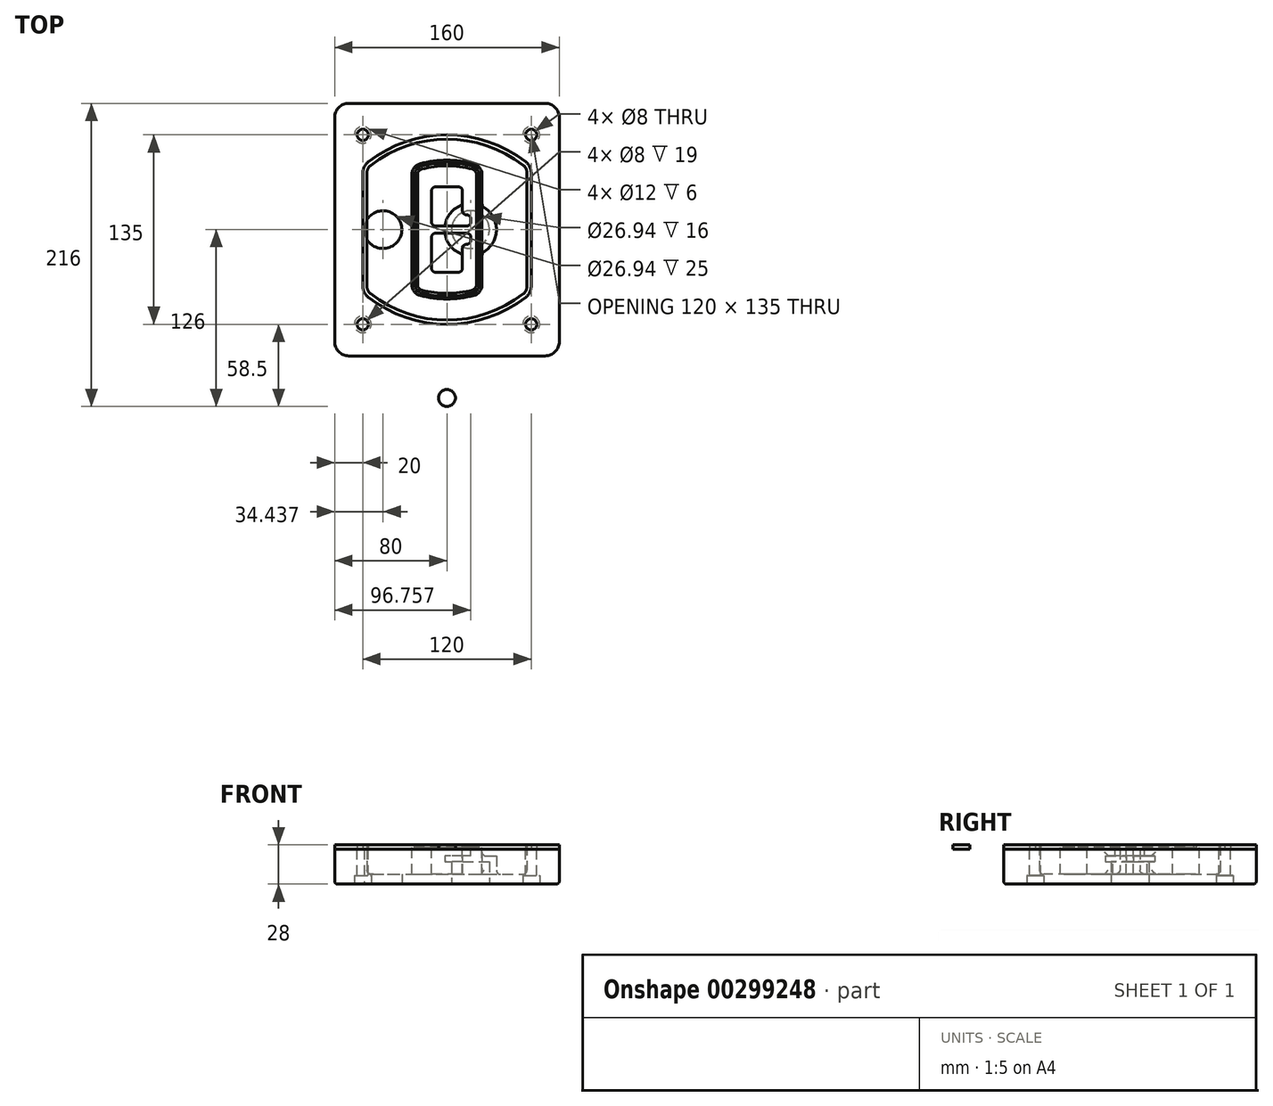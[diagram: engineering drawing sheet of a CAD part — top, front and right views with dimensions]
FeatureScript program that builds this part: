
annotation { "Feature Type Name" : "Feature", "Feature Type Description" : "" }
export const myFeature = defineFeature(function(context is Context, id is Id, definition is map)
    precondition{}
    {
        {
            var Q0;
            Q0=qCreatedBy(makeId("Top.planeOp"),FACE);
            var sketch = newSketch(context, id + "F0", { "sketchPlane" : qUnion([Q0])});
            skPoint(sketch, "E0.rect.middle", {"position": v(0, 0) * mm});
            skLineSegment(sketch, "E1.bottom", {"start": v(-70, -90) * mm, "end": v(70, -90) * mm});
            skLineSegment(sketch, "E1.top", {"start": v(-70, 90) * mm, "end": v(70, 90) * mm});
            skLineSegment(sketch, "E1.left", {"start": v(-80, -80) * mm, "end": v(-80, 80) * mm});
            skLineSegment(sketch, "E1.right", {"start": v(80, -80) * mm, "end": v(80, 80) * mm});
            skLineSegment(sketch, "E2", {"start": v(-80, 90) * mm, "end": v(80, -90) * mm, "construction": true});
            skLineSegment(sketch, "E3", {"start": v(80, 90) * mm, "end": v(-80, -90) * mm, "construction": true});
            skCircle(sketch, "E4", {"center": v(-60, 67.5) * mm, "radius": 4 * mm});
            skCircle(sketch, "E5", {"center": v(60, 67.5) * mm, "radius": 4 * mm});
            skCircle(sketch, "E6", {"center": v(60, -67.5) * mm, "radius": 4 * mm});
            skCircle(sketch, "E7", {"center": v(-60, -67.5) * mm, "radius": 4 * mm});
            skLineSegment(sketch, "E8", {"start": v(-60, 67.5) * mm, "end": v(60, 67.5) * mm, "construction": true});
            skLineSegment(sketch, "E9", {"start": v(60, 67.5) * mm, "end": v(60, -67.5) * mm, "construction": true});
            skLineSegment(sketch, "E10", {"start": v(60, -67.5) * mm, "end": v(-60, -67.5) * mm, "construction": true});
            skLineSegment(sketch, "E11", {"start": v(-60, -67.5) * mm, "end": v(-60, 67.5) * mm, "construction": true});
            skLineSegment(sketch, "E12", {"start": v(-60, 40.3) * mm, "end": v(-60, -40.3) * mm});
            skLineSegment(sketch, "E13", {"start": v(60, 40.3) * mm, "end": v(60, -40.3) * mm});
            skArc(sketch, "E14", {"start": v(56.15, 48.18) * mm, "mid": v(0, 67.5) * mm, "end": v(-56.15, 48.18) * mm});
            skArc(sketch, "E15", {"start": v(-56.15, -48.18) * mm, "mid": v(0, -67.5) * mm, "end": v(56.15, -48.18) * mm});
            skLineSegment(sketch, "E16", {"start": v(-60, 0) * mm, "end": v(60, 0) * mm, "construction": true});
            skPoint(sketch, "E17.visualSharp", {"position": v(-60, -45) * mm});
            skArc(sketch, "E17.filletArc", {"start": v(-60, -40.3) * mm, "mid": v(-58.99, -44.68) * mm, "end": v(-56.15, -48.18) * mm});
            skPoint(sketch, "E18.visualSharp", {"position": v(-60, 45) * mm});
            skArc(sketch, "E18.filletArc", {"start": v(-56.15, 48.18) * mm, "mid": v(-58.99, 44.68) * mm, "end": v(-60, 40.3) * mm});
            skPoint(sketch, "E19.visualSharp", {"position": v(60, 45) * mm});
            skArc(sketch, "E19.filletArc", {"start": v(60, 40.3) * mm, "mid": v(58.99, 44.68) * mm, "end": v(56.15, 48.18) * mm});
            skPoint(sketch, "E20.visualSharp", {"position": v(60, -45) * mm});
            skArc(sketch, "E20.filletArc", {"start": v(56.15, -48.18) * mm, "mid": v(58.99, -44.68) * mm, "end": v(60, -40.3) * mm});
            skPoint(sketch, "E21.visualSharp", {"position": v(-80, 90) * mm});
            skArc(sketch, "E21.filletArc", {"start": v(-70, 90) * mm, "mid": v(-77.07, 87.07) * mm, "end": v(-80, 80) * mm});
            skPoint(sketch, "E22.visualSharp", {"position": v(80, 90) * mm});
            skArc(sketch, "E22.filletArc", {"start": v(80, 80) * mm, "mid": v(77.07, 87.07) * mm, "end": v(70, 90) * mm});
            skPoint(sketch, "E23.visualSharp", {"position": v(80, -90) * mm});
            skArc(sketch, "E23.filletArc", {"start": v(70, -90) * mm, "mid": v(77.07, -87.07) * mm, "end": v(80, -80) * mm});
            skPoint(sketch, "E24.visualSharp", {"position": v(-80, -90) * mm});
            skArc(sketch, "E24.filletArc", {"start": v(-80, -80) * mm, "mid": v(-77.07, -87.07) * mm, "end": v(-70, -90) * mm});
            skArc(sketch, "E25.0", {"start": v(57, 40.3) * mm, "mid": v(56.3, 43.36) * mm, "end": v(54.3, 45.81) * mm});
            skLineSegment(sketch, "E25.1", {"start": v(57, 40.3) * mm, "end": v(57, -40.3) * mm});
            skArc(sketch, "E25.2", {"start": v(54.3, -45.81) * mm, "mid": v(56.3, -43.36) * mm, "end": v(57, -40.3) * mm});
            skArc(sketch, "E25.3", {"start": v(-54.3, -45.81) * mm, "mid": v(0, -64.5) * mm, "end": v(54.3, -45.81) * mm});
            skArc(sketch, "E25.4", {"start": v(-57, -40.3) * mm, "mid": v(-56.3, -43.36) * mm, "end": v(-54.3, -45.81) * mm});
            skArc(sketch, "E25.5", {"start": v(54.3, 45.81) * mm, "mid": v(0, 64.5) * mm, "end": v(-54.3, 45.81) * mm});
            skLineSegment(sketch, "E25.6", {"start": v(-57, 40.3) * mm, "end": v(-57, -40.3) * mm});
            skArc(sketch, "E25.7", {"start": v(-54.3, 45.81) * mm, "mid": v(-56.3, 43.36) * mm, "end": v(-57, 40.3) * mm});
            skArc(sketch, "E26.0", {"start": v(-58.62, 51.33) * mm, "mid": v(-62.58, 46.43) * mm, "end": v(-64, 40.3) * mm});
            skArc(sketch, "E26.1", {"start": v(58.62, 51.33) * mm, "mid": v(0, 71.5) * mm, "end": v(-58.62, 51.33) * mm});
            skArc(sketch, "E26.2", {"start": v(64, 40.3) * mm, "mid": v(62.58, 46.43) * mm, "end": v(58.62, 51.33) * mm});
            skLineSegment(sketch, "E26.3", {"start": v(64, 40.3) * mm, "end": v(64, -40.3) * mm});
            skArc(sketch, "E26.4", {"start": v(58.62, -51.33) * mm, "mid": v(62.58, -46.43) * mm, "end": v(64, -40.3) * mm});
            skLineSegment(sketch, "E26.5", {"start": v(-64, 40.3) * mm, "end": v(-64, -40.3) * mm});
            skArc(sketch, "E26.6", {"start": v(-58.62, -51.33) * mm, "mid": v(0, -71.5) * mm, "end": v(58.62, -51.33) * mm});
            skArc(sketch, "E26.7", {"start": v(-64, -40.3) * mm, "mid": v(-62.58, -46.43) * mm, "end": v(-58.62, -51.33) * mm});
            skSolve(sketch);
        }
        {
            var Q0;
            Q0=makeQuery(id+"F0.imprint","IMPRINT",FACE,{"disambiguationData":[TD([[makeQuery(id+"F0.imprint","IMPRINT",EDGE,{"derivedFrom":sQuery(id+"F0.wireOp",EDGE,"E1.bottom")}),1.0]])]});
            var Q1;
            Q1=makeQuery(id+"F0.imprint","IMPRINT",FACE,{"disambiguationData":[TD([[makeQuery(id+"F0.imprint","IMPRINT",EDGE,{"derivedFrom":sQuery(id+"F0.wireOp",EDGE,"E12")}),1.0]])]});
            var Q2;
            Q2=makeQuery(id+"F0.imprint","IMPRINT",FACE,{"disambiguationData":[TD([[makeQuery(id+"F0.imprint","IMPRINT",EDGE,{"derivedFrom":sQuery(id+"F0.wireOp",EDGE,"E25.0")}),1.0]])]});
            var Q3;
            Q3=makeQuery(id+"F0.imprint","IMPRINT",FACE,{"disambiguationData":[TD([[makeQuery(id+"F0.imprint","IMPRINT",EDGE,{"derivedFrom":sQuery(id+"F0.wireOp",EDGE,"E12")}),-1.0]])]});
            extrude(context, id + "F1", {"entities" : qUnion([Q0, Q1, Q2, Q3]), "oppositeDirection" : true, "depth" : 25 * mm});
        }
        {
            var Q0;
            Q0=makeQuery(id+"F0.imprint","IMPRINT",FACE,{"disambiguationData":[TD([[makeQuery(id+"F0.imprint","IMPRINT",EDGE,{"derivedFrom":sQuery(id+"F0.wireOp",EDGE,"E12")}),1.0]])]});
            extrude(context, id + "F2", {"entities" : qUnion([Q0]), "operationType" : NewBodyOperationType.ADD, "depth" : 3 * mm});
        }
        {
            var Q0;
            Q0=makeQuery(id+"F0.imprint","IMPRINT",FACE,{"disambiguationData":[TD([[makeQuery(id+"F0.imprint","IMPRINT",EDGE,{"derivedFrom":sQuery(id+"F0.wireOp",EDGE,"E25.0")}),1.0]])]});
            extrude(context, id + "F3", {"entities" : qUnion([Q0]), "operationType" : NewBodyOperationType.REMOVE, "oppositeDirection" : true, "depth" : 18 * mm});
        }
        {
            var Q0;
            Q0=makeQuery(id+"F2.opExtrude","CAP_FACE",FACE,{"disambiguationData":[OSD([sQuery(id+"F0.wireOp",EDGE,"E12"),sQuery(id+"F0.wireOp",EDGE,"E13"),sQuery(id+"F0.wireOp",EDGE,"E14"),sQuery(id+"F0.wireOp",EDGE,"E15"),sQuery(id+"F0.wireOp",EDGE,"E17.filletArc"),sQuery(id+"F0.wireOp",EDGE,"E18.filletArc"),sQuery(id+"F0.wireOp",EDGE,"E19.filletArc"),sQuery(id+"F0.wireOp",EDGE,"E20.filletArc"),sQuery(id+"F0.wireOp",EDGE,"E25.0"),sQuery(id+"F0.wireOp",EDGE,"E25.1"),sQuery(id+"F0.wireOp",EDGE,"E25.2"),sQuery(id+"F0.wireOp",EDGE,"E25.3"),sQuery(id+"F0.wireOp",EDGE,"E25.4"),sQuery(id+"F0.wireOp",EDGE,"E25.5"),sQuery(id+"F0.wireOp",EDGE,"E25.6"),sQuery(id+"F0.wireOp",EDGE,"E25.7")])],"isStart":false});
            var sketch = newSketch(context, id + "F4", { "sketchPlane" : qUnion([Q0])});
            skArc(sketch, "E27.0", {"start": v(-19.08, -46.97) * mm, "mid": v(0, -49.5) * mm, "end": v(19.08, -46.97) * mm});
            skArc(sketch, "E28.0", {"start": v(19.08, 46.97) * mm, "mid": v(0, 49.5) * mm, "end": v(-19.08, 46.97) * mm});
            skLineSegment(sketch, "E29", {"start": v(-25, 39.25) * mm, "end": v(-25, -39.25) * mm});
            skLineSegment(sketch, "E30", {"start": v(25, 39.25) * mm, "end": v(25, -39.25) * mm});
            skLineSegment(sketch, "E31", {"start": v(-25, 45.1) * mm, "end": v(25, 45.1) * mm, "construction": true});
            skLineSegment(sketch, "E32", {"start": v(-25, -45.1) * mm, "end": v(25, -45.1) * mm, "construction": true});
            skPoint(sketch, "E33.visualSharp", {"position": v(-25, 45.1) * mm});
            skArc(sketch, "E33.filletArc", {"start": v(-19.08, 46.97) * mm, "mid": v(-23.35, 44.11) * mm, "end": v(-25, 39.25) * mm});
            skPoint(sketch, "E34.visualSharp", {"position": v(25, 45.1) * mm});
            skArc(sketch, "E34.filletArc", {"start": v(25, 39.25) * mm, "mid": v(23.35, 44.11) * mm, "end": v(19.08, 46.97) * mm});
            skPoint(sketch, "E35.visualSharp", {"position": v(25, -45.1) * mm});
            skArc(sketch, "E35.filletArc", {"start": v(19.08, -46.97) * mm, "mid": v(23.35, -44.11) * mm, "end": v(25, -39.25) * mm});
            skPoint(sketch, "E36.visualSharp", {"position": v(-25, -45.1) * mm});
            skArc(sketch, "E36.filletArc", {"start": v(-25, -39.25) * mm, "mid": v(-23.35, -44.11) * mm, "end": v(-19.08, -46.97) * mm});
            skArc(sketch, "E37.0", {"start": v(54.3, 45.81) * mm, "mid": v(0, 64.5) * mm, "end": v(-54.3, 45.81) * mm});
            skArc(sketch, "E37.1", {"start": v(-54.3, 45.81) * mm, "mid": v(-56.3, 43.36) * mm, "end": v(-57, 40.3) * mm});
            skLineSegment(sketch, "E37.2", {"start": v(-57, 40.3) * mm, "end": v(-57, -40.3) * mm});
            skArc(sketch, "E37.3", {"start": v(-57, -40.3) * mm, "mid": v(-56.3, -43.36) * mm, "end": v(-54.3, -45.81) * mm});
            skArc(sketch, "E37.4", {"start": v(-54.3, -45.81) * mm, "mid": v(0, -64.5) * mm, "end": v(54.3, -45.81) * mm});
            skArc(sketch, "E37.5", {"start": v(54.3, -45.81) * mm, "mid": v(56.3, -43.36) * mm, "end": v(57, -40.3) * mm});
            skLineSegment(sketch, "E37.6", {"start": v(57, 40.3) * mm, "end": v(57, -40.3) * mm});
            skArc(sketch, "E37.7", {"start": v(57, 40.3) * mm, "mid": v(56.3, 43.36) * mm, "end": v(54.3, 45.81) * mm});
            skLineSegment(sketch, "E38.0", {"start": v(23, 39.25) * mm, "end": v(23, -39.25) * mm});
            skArc(sketch, "E38.1", {"start": v(18.56, -45.04) * mm, "mid": v(21.76, -42.9) * mm, "end": v(23, -39.25) * mm});
            skArc(sketch, "E38.2", {"start": v(-18.56, -45.04) * mm, "mid": v(0, -47.5) * mm, "end": v(18.56, -45.04) * mm});
            skArc(sketch, "E38.3", {"start": v(-23, -39.25) * mm, "mid": v(-21.76, -42.9) * mm, "end": v(-18.56, -45.04) * mm});
            skLineSegment(sketch, "E38.4", {"start": v(-23, 39.25) * mm, "end": v(-23, -39.25) * mm});
            skArc(sketch, "E38.5", {"start": v(23, 39.25) * mm, "mid": v(21.76, 42.9) * mm, "end": v(18.56, 45.04) * mm});
            skArc(sketch, "E38.6", {"start": v(-18.56, 45.04) * mm, "mid": v(-21.76, 42.9) * mm, "end": v(-23, 39.25) * mm});
            skArc(sketch, "E38.7", {"start": v(18.56, 45.04) * mm, "mid": v(0, 47.5) * mm, "end": v(-18.56, 45.04) * mm});
            skArc(sketch, "E39.0", {"start": v(21, 39.25) * mm, "mid": v(20.18, 41.68) * mm, "end": v(18.04, 43.1) * mm});
            skLineSegment(sketch, "E39.1", {"start": v(21, 39.25) * mm, "end": v(21, -39.25) * mm});
            skArc(sketch, "E39.2", {"start": v(18.04, -43.1) * mm, "mid": v(20.18, -41.68) * mm, "end": v(21, -39.25) * mm});
            skArc(sketch, "E39.3", {"start": v(-18.04, -43.1) * mm, "mid": v(0, -45.5) * mm, "end": v(18.04, -43.1) * mm});
            skArc(sketch, "E39.4", {"start": v(-21, -39.25) * mm, "mid": v(-20.18, -41.68) * mm, "end": v(-18.04, -43.1) * mm});
            skArc(sketch, "E39.5", {"start": v(18.04, 43.1) * mm, "mid": v(0, 45.5) * mm, "end": v(-18.04, 43.1) * mm});
            skLineSegment(sketch, "E39.6", {"start": v(-21, 39.25) * mm, "end": v(-21, -39.25) * mm});
            skArc(sketch, "E39.7", {"start": v(-18.04, 43.1) * mm, "mid": v(-20.18, 41.68) * mm, "end": v(-21, 39.25) * mm});
            skLineSegment(sketch, "E40", {"start": v(-25, 0) * mm, "end": v(25, 0) * mm, "construction": true});
            skLineSegment(sketch, "E41", {"start": v(-11, 5.5) * mm, "end": v(-11, 27.5) * mm});
            skLineSegment(sketch, "E42", {"start": v(-8, 30.5) * mm, "end": v(8, 30.5) * mm});
            skLineSegment(sketch, "E43", {"start": v(11, 27.5) * mm, "end": v(11, 13.5) * mm});
            skLineSegment(sketch, "E44", {"start": v(14, 10.5) * mm, "end": v(14, 10.5) * mm});
            skLineSegment(sketch, "E45", {"start": v(17, 7.5) * mm, "end": v(17, 5.5) * mm});
            skLineSegment(sketch, "E46", {"start": v(14, 2.5) * mm, "end": v(-8, 2.5) * mm});
            skPoint(sketch, "E47.visualSharp", {"position": v(-11, 30.5) * mm});
            skArc(sketch, "E47.filletArc", {"start": v(-8, 30.5) * mm, "mid": v(-10.12, 29.62) * mm, "end": v(-11, 27.5) * mm});
            skPoint(sketch, "E48.visualSharp", {"position": v(11, 30.5) * mm});
            skArc(sketch, "E48.filletArc", {"start": v(11, 27.5) * mm, "mid": v(10.12, 29.62) * mm, "end": v(8, 30.5) * mm});
            skPoint(sketch, "E49.visualSharp", {"position": v(11, 10.5) * mm});
            skArc(sketch, "E49.filletArc", {"start": v(11, 13.5) * mm, "mid": v(11.88, 11.38) * mm, "end": v(14, 10.5) * mm});
            skPoint(sketch, "E50.visualSharp", {"position": v(17, 10.5) * mm});
            skArc(sketch, "E50.filletArc", {"start": v(17, 7.5) * mm, "mid": v(16.12, 9.62) * mm, "end": v(14, 10.5) * mm});
            skPoint(sketch, "E51.visualSharp", {"position": v(17, 2.5) * mm});
            skArc(sketch, "E51.filletArc", {"start": v(14, 2.5) * mm, "mid": v(16.12, 3.38) * mm, "end": v(17, 5.5) * mm});
            skPoint(sketch, "E52.visualSharp", {"position": v(-11, 2.5) * mm});
            skArc(sketch, "E52.filletArc", {"start": v(-11, 5.5) * mm, "mid": v(-10.12, 3.38) * mm, "end": v(-8, 2.5) * mm});
            skLineSegment(sketch, "E53.0.MirrorCS", {"start": v(14, -2.5) * mm, "end": v(-8, -2.5) * mm});
            skArc(sketch, "E54.0.MirrorCS", {"start": v(-11, -5.5) * mm, "mid": v(-10.12, -3.38) * mm, "end": v(-8, -2.5) * mm});
            skLineSegment(sketch, "E55.0.MirrorCS", {"start": v(-11, -5.5) * mm, "end": v(-11, -27.5) * mm});
            skArc(sketch, "E56.0.MirrorCS", {"start": v(-8, -30.5) * mm, "mid": v(-10.12, -29.62) * mm, "end": v(-11, -27.5) * mm});
            skLineSegment(sketch, "E57.0.MirrorCS", {"start": v(-8, -30.5) * mm, "end": v(8, -30.5) * mm});
            skArc(sketch, "E58.0.MirrorCS", {"start": v(11, -27.5) * mm, "mid": v(10.12, -29.62) * mm, "end": v(8, -30.5) * mm});
            skLineSegment(sketch, "E59.0.MirrorCS", {"start": v(11, -27.5) * mm, "end": v(11, -13.5) * mm});
            skArc(sketch, "E60.0.MirrorCS", {"start": v(11, -13.5) * mm, "mid": v(11.88, -11.38) * mm, "end": v(14, -10.5) * mm});
            skArc(sketch, "E61.0.MirrorCS", {"start": v(17, -7.5) * mm, "mid": v(16.12, -9.62) * mm, "end": v(14, -10.5) * mm});
            skLineSegment(sketch, "E62.0.MirrorCS", {"start": v(17, -7.5) * mm, "end": v(17, -5.5) * mm});
            skArc(sketch, "E63.0.MirrorCS", {"start": v(14, -2.5) * mm, "mid": v(16.12, -3.38) * mm, "end": v(17, -5.5) * mm});
            skSolve(sketch);
        }
        {
            var Q0;
            Q0=makeQuery(id+"F4.imprint","IMPRINT",FACE,{"disambiguationData":[TD([[makeQuery(id+"F4.imprint","IMPRINT",EDGE,{"derivedFrom":sQuery(id+"F4.wireOp",EDGE,"E27.0")}),1.0]])]});
            var Q1;
            Q1=makeQuery(id+"F4.imprint","IMPRINT",FACE,{"disambiguationData":[TD([[makeQuery(id+"F4.imprint","IMPRINT",EDGE,{"derivedFrom":sQuery(id+"F4.wireOp",EDGE,"E38.0")}),-1.0]])]});
            var Q2;
            Q2=makeQuery(id+"F4.imprint","IMPRINT",FACE,{"disambiguationData":[TD([[makeQuery(id+"F4.imprint","IMPRINT",EDGE,{"derivedFrom":sQuery(id+"F4.wireOp",EDGE,"E39.0")}),1.0]])]});
            extrude(context, id + "F5", {"entities" : qUnion([Q0, Q1, Q2]), "operationType" : NewBodyOperationType.ADD, "endBound" : BoundingType.UP_TO_NEXT, "oppositeDirection" : true, "depth" : 25 * mm});
        }
        {
            var Q0;
            Q0=makeQuery(id+"F4.imprint","IMPRINT",FACE,{"disambiguationData":[TD([[makeQuery(id+"F4.imprint","IMPRINT",EDGE,{"derivedFrom":sQuery(id+"F4.wireOp",EDGE,"E38.0")}),-1.0]])]});
            extrude(context, id + "F6", {"entities" : qUnion([Q0]), "operationType" : NewBodyOperationType.REMOVE, "oppositeDirection" : true, "depth" : 2 * mm});
        }
        {
            var Q0;
            Q0=makeQuery(id+"F1.opExtrude","CAP_FACE",FACE,{"disambiguationData":[OSD([sQuery(id+"F0.wireOp",EDGE,"E1.bottom"),sQuery(id+"F0.wireOp",EDGE,"E1.top"),sQuery(id+"F0.wireOp",EDGE,"E1.left"),sQuery(id+"F0.wireOp",EDGE,"E1.right"),sQuery(id+"F0.wireOp",EDGE,"E4"),sQuery(id+"F0.wireOp",EDGE,"E5"),sQuery(id+"F0.wireOp",EDGE,"E6"),sQuery(id+"F0.wireOp",EDGE,"E7"),sQuery(id+"F0.wireOp",EDGE,"E21.filletArc"),sQuery(id+"F0.wireOp",EDGE,"E22.filletArc"),sQuery(id+"F0.wireOp",EDGE,"E23.filletArc"),sQuery(id+"F0.wireOp",EDGE,"E24.filletArc")])],"isStart":false});
            var sketch = newSketch(context, id + "F7", { "sketchPlane" : qUnion([Q0])});
            skCircle(sketch, "E64", {"center": v(16.76, 0) * mm, "radius": 13.47 * mm});
            skCircle(sketch, "E65", {"center": v(-45.56, 0) * mm, "radius": 13.47 * mm});
            skLineSegment(sketch, "E66", {"start": v(80, 0) * mm, "end": v(-80, 0) * mm});
            skCircle(sketch, "E67", {"center": v(16.76, 0) * mm, "radius": 18.47 * mm});
            skCircle(sketch, "E68", {"center": v(60, -67.5) * mm, "radius": 6 * mm});
            skCircle(sketch, "E69", {"center": v(-60, -67.5) * mm, "radius": 6 * mm});
            skCircle(sketch, "E70", {"center": v(-60, 67.5) * mm, "radius": 6 * mm});
            skCircle(sketch, "E71", {"center": v(60, 67.5) * mm, "radius": 6 * mm});
            skSolve(sketch);
        }
        {
            var Q0;
            {var subQ1=sQuery(id+"F7.wireOp",EDGE,"E66");var subQ4=sQuery(id+"F7.wireOp",EDGE,"E64");var subQ6=makeQuery(id+"F7.imprint","INTERSECT",VERTEX,{"disambiguationData":[OD(0.0)],"derivedFrom":[subQ4,subQ1]});Q0=makeQuery(id+"F7.imprint","IMPRINT",FACE,{"disambiguationData":[TD([[makeQuery(id+"F7.imprint","IMPRINT",EDGE,{"disambiguationData":[TD([[subQ6,-1.0]])],"derivedFrom":subQ4}),-1.0]])]});}
            var Q1;
            {var subQ0=sQuery(id+"F7.wireOp",EDGE,"E66");var subQ1=sQuery(id+"F7.wireOp",EDGE,"E64");var subQ3=makeQuery(id+"F7.imprint","INTERSECT",VERTEX,{"disambiguationData":[OD(0.0)],"derivedFrom":[subQ1,subQ0]});Q1=makeQuery(id+"F7.imprint","IMPRINT",FACE,{"disambiguationData":[TD([[makeQuery(id+"F7.imprint","IMPRINT",EDGE,{"disambiguationData":[TD([[subQ3,-1.0]])],"derivedFrom":subQ1}),1.0]])]});}
            var Q2;
            {var subQ0=sQuery(id+"F7.wireOp",EDGE,"E66");var subQ1=sQuery(id+"F7.wireOp",EDGE,"E64");var subQ3=makeQuery(id+"F7.imprint","INTERSECT",VERTEX,{"disambiguationData":[OD(0.0)],"derivedFrom":[subQ1,subQ0]});Q2=makeQuery(id+"F7.imprint","IMPRINT",FACE,{"disambiguationData":[TD([[makeQuery(id+"F7.imprint","IMPRINT",EDGE,{"disambiguationData":[TD([[subQ3,1.0]])],"derivedFrom":subQ1}),1.0]])]});}
            var Q3;
            {var subQ1=sQuery(id+"F7.wireOp",EDGE,"E66");var subQ4=sQuery(id+"F7.wireOp",EDGE,"E64");var subQ6=makeQuery(id+"F7.imprint","INTERSECT",VERTEX,{"disambiguationData":[OD(0.0)],"derivedFrom":[subQ4,subQ1]});Q3=makeQuery(id+"F7.imprint","IMPRINT",FACE,{"disambiguationData":[TD([[makeQuery(id+"F7.imprint","IMPRINT",EDGE,{"disambiguationData":[TD([[subQ6,1.0]])],"derivedFrom":subQ4}),-1.0]])]});}
            extrude(context, id + "F8", {"entities" : qUnion([Q0, Q1, Q2, Q3]), "operationType" : NewBodyOperationType.ADD, "oppositeDirection" : true, "depth" : 20 * mm});
        }
        {
            var Q0;
            {var subQ0=sQuery(id+"F7.wireOp",EDGE,"E66");var subQ1=sQuery(id+"F7.wireOp",EDGE,"E64");var subQ3=makeQuery(id+"F7.imprint","INTERSECT",VERTEX,{"disambiguationData":[OD(0.0)],"derivedFrom":[subQ1,subQ0]});Q0=makeQuery(id+"F7.imprint","IMPRINT",FACE,{"disambiguationData":[TD([[makeQuery(id+"F7.imprint","IMPRINT",EDGE,{"disambiguationData":[TD([[subQ3,-1.0]])],"derivedFrom":subQ1}),1.0]])]});}
            var Q1;
            {var subQ0=sQuery(id+"F7.wireOp",EDGE,"E66");var subQ1=sQuery(id+"F7.wireOp",EDGE,"E64");var subQ3=makeQuery(id+"F7.imprint","INTERSECT",VERTEX,{"disambiguationData":[OD(0.0)],"derivedFrom":[subQ1,subQ0]});Q1=makeQuery(id+"F7.imprint","IMPRINT",FACE,{"disambiguationData":[TD([[makeQuery(id+"F7.imprint","IMPRINT",EDGE,{"disambiguationData":[TD([[subQ3,1.0]])],"derivedFrom":subQ1}),1.0]])]});}
            extrude(context, id + "F9", {"entities" : qUnion([Q0, Q1]), "operationType" : NewBodyOperationType.REMOVE, "oppositeDirection" : true, "depth" : 16 * mm});
        }
        {
            var Q0;
            {var subQ0=sQuery(id+"F7.wireOp",EDGE,"E66");var subQ1=sQuery(id+"F7.wireOp",EDGE,"E65");var subQ3=makeQuery(id+"F7.imprint","INTERSECT",VERTEX,{"disambiguationData":[OD(0.0)],"derivedFrom":[subQ1,subQ0]});Q0=makeQuery(id+"F7.imprint","IMPRINT",FACE,{"disambiguationData":[TD([[makeQuery(id+"F7.imprint","IMPRINT",EDGE,{"disambiguationData":[TD([[subQ3,-1.0]])],"derivedFrom":subQ1}),1.0]])]});}
            var Q1;
            {var subQ0=sQuery(id+"F7.wireOp",EDGE,"E66");var subQ1=sQuery(id+"F7.wireOp",EDGE,"E65");var subQ3=makeQuery(id+"F7.imprint","INTERSECT",VERTEX,{"disambiguationData":[OD(0.0)],"derivedFrom":[subQ1,subQ0]});Q1=makeQuery(id+"F7.imprint","IMPRINT",FACE,{"disambiguationData":[TD([[makeQuery(id+"F7.imprint","IMPRINT",EDGE,{"disambiguationData":[TD([[subQ3,1.0]])],"derivedFrom":subQ1}),1.0]])]});}
            extrude(context, id + "F10", {"entities" : qUnion([Q0, Q1]), "operationType" : NewBodyOperationType.REMOVE, "oppositeDirection" : true, "depth" : 25 * mm});
        }
        {
            var Q0;
            Q0=makeQuery(id+"F9.boolean.opBoolean","COPY",FACE,{"derivedFrom":makeQuery(id+"F9.opExtrude","CAP_FACE",FACE,{"disambiguationData":[OSD([sQuery(id+"F7.wireOp",EDGE,"E64")])],"isStart":false})});
            var sketch = newSketch(context, id + "F11", { "sketchPlane" : qUnion([Q0])});
            skArc(sketch, "E72.0", {"start": v(11, 17.55) * mm, "mid": v(2.57, 11.82) * mm, "end": v(-1.54, 2.5) * mm});
            skArc(sketch, "E72.1", {"start": v(-1.54, -2.5) * mm, "mid": v(2.57, -11.82) * mm, "end": v(11, -17.55) * mm});
            skLineSegment(sketch, "E73", {"start": v(-1.54, -2.5) * mm, "end": v(14, -2.5) * mm});
            skLineSegment(sketch, "E74.0", {"start": v(14, 2.5) * mm, "end": v(-1.54, 2.5) * mm});
            skArc(sketch, "E74.1", {"start": v(14, 2.5) * mm, "mid": v(16.12, 3.38) * mm, "end": v(17, 5.5) * mm});
            skLineSegment(sketch, "E74.2", {"start": v(17, 7.5) * mm, "end": v(17, 5.5) * mm});
            skArc(sketch, "E74.3", {"start": v(17, 7.5) * mm, "mid": v(16.12, 9.62) * mm, "end": v(14, 10.5) * mm});
            skArc(sketch, "E74.4", {"start": v(11, 13.5) * mm, "mid": v(11.88, 11.38) * mm, "end": v(14, 10.5) * mm});
            skLineSegment(sketch, "E74.5", {"start": v(11, 17.55) * mm, "end": v(11, 13.5) * mm});
            skLineSegment(sketch, "E74.7", {"start": v(14, -2.5) * mm, "end": v(-1.54, -2.5) * mm});
            skArc(sketch, "E74.8", {"start": v(14, -2.5) * mm, "mid": v(16.12, -3.38) * mm, "end": v(17, -5.5) * mm});
            skLineSegment(sketch, "E74.9", {"start": v(17, -7.5) * mm, "end": v(17, -5.5) * mm});
            skArc(sketch, "E74.10", {"start": v(17, -7.5) * mm, "mid": v(16.12, -9.62) * mm, "end": v(14, -10.5) * mm});
            skArc(sketch, "E74.11", {"start": v(11, -13.5) * mm, "mid": v(11.88, -11.38) * mm, "end": v(14, -10.5) * mm});
            skLineSegment(sketch, "E74.12", {"start": v(11, -17.55) * mm, "end": v(11, -13.5) * mm});
            skPoint(sketch, "E75.orphan", {"position": v(11, -27.5) * mm});
            skPoint(sketch, "E76.orphan", {"position": v(-8, -2.5) * mm});
            skPoint(sketch, "E77.orphan", {"position": v(-8, 2.5) * mm});
            skPoint(sketch, "E78.orphan", {"position": v(11, 27.5) * mm});
            skSolve(sketch);
        }
        {
            var Q0;
            Q0=makeQuery(id+"F7.imprint","IMPRINT",FACE,{"disambiguationData":[TD([[makeQuery(id+"F7.imprint","IMPRINT",EDGE,{"derivedFrom":sQuery(id+"F7.wireOp",EDGE,"E68")}),1.0]])]});
            var Q1;
            Q1=makeQuery(id+"F7.imprint","IMPRINT",FACE,{"disambiguationData":[TD([[makeQuery(id+"F7.imprint","IMPRINT",EDGE,{"derivedFrom":makeQuery(id+"F1.opExtrude","CAP_EDGE",EDGE,{"disambiguationData":[OSD([sQuery(id+"F0.wireOp",EDGE,"E5")])],"isStart":false})}),-1.0]])]});
            var Q2;
            Q2=makeQuery(id+"F7.imprint","IMPRINT",FACE,{"disambiguationData":[TD([[makeQuery(id+"F7.imprint","IMPRINT",EDGE,{"derivedFrom":sQuery(id+"F7.wireOp",EDGE,"E69")}),1.0]])]});
            var Q3;
            Q3=makeQuery(id+"F7.imprint","IMPRINT",FACE,{"disambiguationData":[TD([[makeQuery(id+"F7.imprint","IMPRINT",EDGE,{"derivedFrom":makeQuery(id+"F1.opExtrude","CAP_EDGE",EDGE,{"disambiguationData":[OSD([sQuery(id+"F0.wireOp",EDGE,"E4")])],"isStart":false})}),-1.0]])]});
            var Q4;
            Q4=makeQuery(id+"F7.imprint","IMPRINT",FACE,{"disambiguationData":[TD([[makeQuery(id+"F7.imprint","IMPRINT",EDGE,{"derivedFrom":sQuery(id+"F7.wireOp",EDGE,"E70")}),1.0]])]});
            var Q5;
            Q5=makeQuery(id+"F7.imprint","IMPRINT",FACE,{"disambiguationData":[TD([[makeQuery(id+"F7.imprint","IMPRINT",EDGE,{"derivedFrom":makeQuery(id+"F1.opExtrude","CAP_EDGE",EDGE,{"disambiguationData":[OSD([sQuery(id+"F0.wireOp",EDGE,"E7")])],"isStart":false})}),-1.0]])]});
            var Q6;
            Q6=makeQuery(id+"F7.imprint","IMPRINT",FACE,{"disambiguationData":[TD([[makeQuery(id+"F7.imprint","IMPRINT",EDGE,{"derivedFrom":sQuery(id+"F7.wireOp",EDGE,"E71")}),1.0]])]});
            var Q7;
            Q7=makeQuery(id+"F7.imprint","IMPRINT",FACE,{"disambiguationData":[TD([[makeQuery(id+"F7.imprint","IMPRINT",EDGE,{"derivedFrom":makeQuery(id+"F1.opExtrude","CAP_EDGE",EDGE,{"disambiguationData":[OSD([sQuery(id+"F0.wireOp",EDGE,"E6")])],"isStart":false})}),-1.0]])]});
            extrude(context, id + "F12", {"entities" : qUnion([Q0, Q1, Q2, Q3, Q4, Q5, Q6, Q7]), "operationType" : NewBodyOperationType.REMOVE, "oppositeDirection" : true, "depth" : 6 * mm});
        }
        {
            var Q0;
            {var subQ7=sQuery(id+"F11.wireOp",EDGE,"E72.0");var subQ14=sQuery(id+"F11.wireOp",EDGE,"E72.1");var subQ16=sQuery(id+"F11.wireOp",EDGE,"E74.1");var subQ18=sQuery(id+"F11.wireOp",EDGE,"E74.8");Q0=qUnion([makeQuery(id+"F11.imprint","IMPRINT",FACE,{"disambiguationData":[TD([[makeQuery(id+"F11.imprint","IMPRINT",EDGE,{"derivedFrom":subQ7}),1.0]])]}),makeQuery(id+"F11.imprint","IMPRINT",FACE,{"disambiguationData":[TD([[makeQuery(id+"F11.imprint","IMPRINT",EDGE,{"derivedFrom":subQ14}),1.0]])]}),makeQuery(id+"F11.imprint","IMPRINT",FACE,{"disambiguationData":[TD([[makeQuery(id+"F11.imprint","IMPRINT",EDGE,{"derivedFrom":subQ16}),1.0]])]}),makeQuery(id+"F11.imprint","IMPRINT",FACE,{"disambiguationData":[TD([[makeQuery(id+"F11.imprint","IMPRINT",EDGE,{"derivedFrom":subQ18}),-1.0]])]})]);}
            var Q1;
            Q1=makeQuery(id+"F5.boolean.opBoolean","SPLIT",FACE,{"disambiguationData":[TD([makeQuery(id+"F5.opExtrude","SWEPT_FACE",FACE,{"disambiguationData":[OSD([sQuery(id+"F4.wireOp",EDGE,"E41")])]})])],"derivedFrom":makeQuery(id+"F3.boolean.opBoolean","COPY",FACE,{"derivedFrom":makeQuery(id+"F3.opExtrude","CAP_FACE",FACE,{"disambiguationData":[OSD([sQuery(id+"F0.wireOp",EDGE,"E25.0"),sQuery(id+"F0.wireOp",EDGE,"E25.1"),sQuery(id+"F0.wireOp",EDGE,"E25.2"),sQuery(id+"F0.wireOp",EDGE,"E25.3"),sQuery(id+"F0.wireOp",EDGE,"E25.4"),sQuery(id+"F0.wireOp",EDGE,"E25.5"),sQuery(id+"F0.wireOp",EDGE,"E25.6"),sQuery(id+"F0.wireOp",EDGE,"E25.7")])],"isStart":false})})});
            extrude(context, id + "F13", {"entities" : qUnion([Q0]), "operationType" : NewBodyOperationType.REMOVE, "endBound" : BoundingType.UP_TO_SURFACE, "endBoundEntityFace" : qUnion([Q1]), "depth" : 25 * mm});
        }
        {
            var Q0;
            Q0=makeQuery(id+"F3.boolean.opBoolean","COPY",EDGE,{"derivedFrom":makeQuery(id+"F3.opExtrude","CAP_EDGE",EDGE,{"disambiguationData":[OSD([sQuery(id+"F0.wireOp",EDGE,"E25.6")])],"isStart":false})});
            var Q1;
            Q1=makeQuery(id+"F8.boolean.opBoolean","INTERSECT",EDGE,{"derivedFrom":[makeQuery(id+"F5.opExtrude","SWEPT_FACE",FACE,{"disambiguationData":[OSD([sQuery(id+"F4.wireOp",EDGE,"E30")])]}),makeQuery(id+"F8.opExtrude","CAP_FACE",FACE,{"disambiguationData":[OSD([sQuery(id+"F7.wireOp",EDGE,"E67")])],"isStart":false})]});
            var Q2;
            Q2=makeQuery(id+"F8.boolean.opBoolean","INTERSECT",EDGE,{"disambiguationData":[OD(1.0)],"derivedFrom":[makeQuery(id+"F5.opExtrude","SWEPT_FACE",FACE,{"disambiguationData":[OSD([sQuery(id+"F4.wireOp",EDGE,"E30")])]}),makeQuery(id+"F8.opExtrude","SWEPT_FACE",FACE,{"disambiguationData":[OSD([sQuery(id+"F7.wireOp",EDGE,"E67")])]})]});
            var Q3;
            {var subQ0=makeQuery(id+"F3.boolean.opBoolean","COPY",FACE,{"derivedFrom":makeQuery(id+"F3.opExtrude","CAP_FACE",FACE,{"disambiguationData":[OSD([sQuery(id+"F0.wireOp",EDGE,"E25.0"),sQuery(id+"F0.wireOp",EDGE,"E25.1"),sQuery(id+"F0.wireOp",EDGE,"E25.2"),sQuery(id+"F0.wireOp",EDGE,"E25.3"),sQuery(id+"F0.wireOp",EDGE,"E25.4"),sQuery(id+"F0.wireOp",EDGE,"E25.5"),sQuery(id+"F0.wireOp",EDGE,"E25.6"),sQuery(id+"F0.wireOp",EDGE,"E25.7")])],"isStart":false})});var subQ1=sQuery(id+"F4.wireOp",EDGE,"E30");Q3=makeQuery(id+"F8.boolean.opBoolean","SPLIT",EDGE,{"disambiguationData":[TD([makeQuery(id+"F5.opExtrude","SWEPT_FACE",FACE,{"disambiguationData":[OSD([sQuery(id+"F4.wireOp",EDGE,"E35.filletArc")])]})])],"derivedFrom":makeQuery(id+"F5.opExtrude","TWEAK_EDGE",EDGE,{"derivedFrom":[subQ0,makeQuery(id+"F4.imprint","IMPRINT",EDGE,{"derivedFrom":subQ1})]})});}
            var Q4;
            {var subQ0=sQuery(id+"F0.wireOp",EDGE,"E25.0");var subQ1=sQuery(id+"F0.wireOp",EDGE,"E25.1");var subQ2=sQuery(id+"F0.wireOp",EDGE,"E25.2");var subQ3=sQuery(id+"F0.wireOp",EDGE,"E25.3");var subQ4=sQuery(id+"F0.wireOp",EDGE,"E25.4");var subQ5=sQuery(id+"F0.wireOp",EDGE,"E25.5");var subQ6=sQuery(id+"F0.wireOp",EDGE,"E25.6");var subQ7=sQuery(id+"F0.wireOp",EDGE,"E25.7");Q4=makeQuery(id+"F8.boolean.opBoolean","INTERSECT",EDGE,{"derivedFrom":[makeQuery(id+"F5.boolean.opBoolean","SPLIT",FACE,{"disambiguationData":[TD([makeQuery(id+"F2.opExtrude","SWEPT_FACE",FACE,{"disambiguationData":[OSD([subQ0])]})])],"derivedFrom":makeQuery(id+"F3.boolean.opBoolean","COPY",FACE,{"derivedFrom":makeQuery(id+"F3.opExtrude","CAP_FACE",FACE,{"disambiguationData":[OSD([subQ0,subQ1,subQ2,subQ3,subQ4,subQ5,subQ6,subQ7])],"isStart":false})})}),makeQuery(id+"F8.opExtrude","SWEPT_FACE",FACE,{"disambiguationData":[OSD([sQuery(id+"F7.wireOp",EDGE,"E67")])]})]});}
            var Q5;
            Q5=makeQuery(id+"F8.boolean.opBoolean","INTERSECT",EDGE,{"disambiguationData":[OD(0.0)],"derivedFrom":[makeQuery(id+"F5.opExtrude","SWEPT_FACE",FACE,{"disambiguationData":[OSD([sQuery(id+"F4.wireOp",EDGE,"E30")])]}),makeQuery(id+"F8.opExtrude","SWEPT_FACE",FACE,{"disambiguationData":[OSD([sQuery(id+"F7.wireOp",EDGE,"E67")])]})]});
            fillet(context, id + "F14", {"entities" : qUnion([Q0, Q1, Q2, Q3, Q4, Q5]), "radius" : 3 * mm, "tangentPropagation" : true, "allowEdgeOverflow" : false});
        }
        {
            var Q0;
            Q0=makeQuery(id+"F1.opExtrude","CAP_EDGE",EDGE,{"disambiguationData":[OSD([sQuery(id+"F0.wireOp",EDGE,"E1.bottom")])],"isStart":false});
            fillet(context, id + "F15", {"entities" : qUnion([Q0]), "radius" : 2 * mm, "tangentPropagation" : true, "allowEdgeOverflow" : false});
        }
        {
            var Q0;
            {var subQ0=sQuery(id+"F0.wireOp",EDGE,"E21.filletArc");var subQ1=sQuery(id+"F0.wireOp",EDGE,"E7");var subQ2=sQuery(id+"F0.wireOp",EDGE,"E6");var subQ3=sQuery(id+"F0.wireOp",EDGE,"E5");var subQ4=sQuery(id+"F0.wireOp",EDGE,"E4");var subQ5=sQuery(id+"F0.wireOp",EDGE,"E22.filletArc");var subQ6=sQuery(id+"F0.wireOp",EDGE,"E1.bottom");var subQ7=sQuery(id+"F0.wireOp",EDGE,"E1.right");var subQ8=sQuery(id+"F0.wireOp",EDGE,"E1.top");var subQ9=sQuery(id+"F0.wireOp",EDGE,"E1.left");var subQ10=sQuery(id+"F0.wireOp",EDGE,"E23.filletArc");var subQ11=sQuery(id+"F0.wireOp",EDGE,"E24.filletArc");Q0=makeQuery(id+"F2.boolean.opBoolean","SPLIT",FACE,{"disambiguationData":[TD([makeQuery(id+"F1.opExtrude","SWEPT_FACE",FACE,{"disambiguationData":[OSD([subQ6])]})])],"derivedFrom":makeQuery(id+"F1.opExtrude","CAP_FACE",FACE,{"disambiguationData":[OSD([subQ6,subQ8,subQ9,subQ7,subQ4,subQ3,subQ2,subQ1,subQ0,subQ5,subQ10,subQ11])],"isStart":true})});}
            var sketch = newSketch(context, id + "F16", { "sketchPlane" : qUnion([Q0])});
            skCircle(sketch, "E79", {"center": v(0, 120) * mm, "radius": 6 * mm});
            skLineSegment(sketch, "E80", {"start": v(-33, 90) * mm, "end": v(-15, 108) * mm});
            skLineSegment(sketch, "E81", {"start": v(-15, 108) * mm, "end": v(-15, 120) * mm});
            skArc(sketch, "E82", {"start": v(15, 120) * mm, "mid": v(0, 135) * mm, "end": v(-15, 120) * mm});
            skLineSegment(sketch, "E83", {"start": v(0, 120) * mm, "end": v(0, 90) * mm, "construction": true});
            skLineSegment(sketch, "E84", {"start": v(15, 120) * mm, "end": v(15, 108) * mm});
            skLineSegment(sketch, "E85", {"start": v(15, 108) * mm, "end": v(33, 90) * mm});
            skLineSegment(sketch, "E86.MirrorCS", {"start": v(33, 90) * mm, "end": v(15, 108) * mm});
            skLineSegment(sketch, "E87.MirrorCS", {"start": v(-15, 108) * mm, "end": v(-33, 90) * mm});
            skLineSegment(sketch, "E88.MirrorCS", {"start": v(15, 108) * mm, "end": v(15, 120) * mm});
            skArc(sketch, "E89.MirrorCS", {"start": v(-15, 120) * mm, "mid": v(0, 135) * mm, "end": v(15, 120) * mm});
            skLineSegment(sketch, "E90.MirrorCS", {"start": v(-15, 120) * mm, "end": v(-15, 108) * mm});
            skLineSegment(sketch, "E91", {"start": v(-80, 0) * mm, "end": v(80, 0) * mm, "construction": true});
            skLineSegment(sketch, "E92.MirrorCS", {"start": v(80, 0) * mm, "end": v(-80, 0) * mm, "construction": true});
            skLineSegment(sketch, "E93.MirrorCS", {"start": v(-15, -108) * mm, "end": v(-15, -120) * mm});
            skLineSegment(sketch, "E94.MirrorCS", {"start": v(15, -120) * mm, "end": v(15, -108) * mm});
            skLineSegment(sketch, "E95.MirrorCS", {"start": v(15, -108) * mm, "end": v(15, -120) * mm});
            skLineSegment(sketch, "E96.MirrorCS", {"start": v(-15, -120) * mm, "end": v(-15, -108) * mm});
            skCircle(sketch, "E97.MirrorC", {"center": v(0, -120) * mm, "radius": 6 * mm});
            skArc(sketch, "E98.MirrorCS", {"start": v(-15, -120) * mm, "mid": v(0, -135) * mm, "end": v(15, -120) * mm});
            skArc(sketch, "E99.MirrorCS", {"start": v(15, -120) * mm, "mid": v(0, -135) * mm, "end": v(-15, -120) * mm});
            skLineSegment(sketch, "E100.MirrorCS", {"start": v(33, -90) * mm, "end": v(15, -108) * mm});
            skLineSegment(sketch, "E101.MirrorCS", {"start": v(15, -108) * mm, "end": v(33, -90) * mm});
            skLineSegment(sketch, "E102.MirrorCS", {"start": v(0, -120) * mm, "end": v(0, -90) * mm, "construction": true});
            skLineSegment(sketch, "E103.MirrorCS", {"start": v(-15, -108) * mm, "end": v(-33, -90) * mm});
            skLineSegment(sketch, "E104.MirrorCS", {"start": v(-33, -90) * mm, "end": v(-15, -108) * mm});
            skSolve(sketch);
        }
        {
            var Q0;
            Q0=makeQuery(id+"F16.imprint","IMPRINT",FACE,{"disambiguationData":[TD([[makeQuery(id+"F16.imprint","IMPRINT",EDGE,{"derivedFrom":sQuery(id+"F16.wireOp",EDGE,"E89.MirrorCS")}),-1.0]])]});
            var Q1;
            Q1=makeQuery(id+"F16.imprint","IMPRINT",FACE,{"disambiguationData":[TD([[makeQuery(id+"F16.imprint","IMPRINT",EDGE,{"derivedFrom":sQuery(id+"F16.wireOp",EDGE,"E97.MirrorC")}),1.0]])]});
            var Q2;
            Q2=makeQuery(id+"F16.imprint","IMPRINT",FACE,{"disambiguationData":[TD([[makeQuery(id+"F16.imprint","IMPRINT",EDGE,{"derivedFrom":makeQuery(id+"F1.opExtrude","CAP_EDGE",EDGE,{"disambiguationData":[OSD([sQuery(id+"F0.wireOp",EDGE,"E1.left")])],"isStart":true})}),-1.0]])]});
            var Q3;
            Q3=makeQuery(id+"F2.opExtrude","CAP_FACE",FACE,{"disambiguationData":[OSD([sQuery(id+"F0.wireOp",EDGE,"E12"),sQuery(id+"F0.wireOp",EDGE,"E13"),sQuery(id+"F0.wireOp",EDGE,"E14"),sQuery(id+"F0.wireOp",EDGE,"E15"),sQuery(id+"F0.wireOp",EDGE,"E17.filletArc"),sQuery(id+"F0.wireOp",EDGE,"E18.filletArc"),sQuery(id+"F0.wireOp",EDGE,"E19.filletArc"),sQuery(id+"F0.wireOp",EDGE,"E20.filletArc"),sQuery(id+"F0.wireOp",EDGE,"E25.0"),sQuery(id+"F0.wireOp",EDGE,"E25.1"),sQuery(id+"F0.wireOp",EDGE,"E25.2"),sQuery(id+"F0.wireOp",EDGE,"E25.3"),sQuery(id+"F0.wireOp",EDGE,"E25.4"),sQuery(id+"F0.wireOp",EDGE,"E25.5"),sQuery(id+"F0.wireOp",EDGE,"E25.6"),sQuery(id+"F0.wireOp",EDGE,"E25.7")])],"isStart":false});
            extrude(context, id + "F17", {"entities" : qUnion([Q0, Q1, Q2]), "endBound" : BoundingType.UP_TO_SURFACE, "endBoundEntityFace" : qUnion([Q3]), "depth" : 25 * mm});
        }
    });
